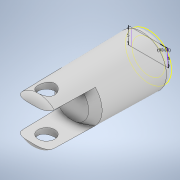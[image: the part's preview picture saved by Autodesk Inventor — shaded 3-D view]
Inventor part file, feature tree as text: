
AUTODESK INVENTOR PART (.ipt)
format: ipt  version: 2021 (Build 250183000, 183)  size: 186,880 bytes
history: native  units: mm
features: sketch x6, extrude x3, fillet x1, chamfer x1
ambient origin geometry x8: Origin, YZ Plane, XZ Plane, XY Plane, X Axis, Y Axis, Z Axis, Center Point
bodies: Solid1 (feature_tree)
feature tree (11):
  extrude  "Extrusion1"  Depth=35.0mm
  fillet  "Fillet1"  Radius=2.0mm
  sketch  "Sketch2"  dims[d4=5.0mm d5=5.0mm]
  sketch  "Sketch3"  dims[d6=90.0deg d7=5.0mm d8=0.0mm d9=0.0mm]
  extrude  "Extrusion2"  Depth=5.0mm
  extrude  "Extrusion4"  Depth=5.0mm
  chamfer  "Chamfer1"  [1 undecoded]
  sketch  "Sketch7"  dims[d16=12.0mm d17=0.0mm d18=2.0mm d19=2.0mm d20=45.0deg]
  sketch  "Sketch1"  dims[d0=15.0mm d1=35.0mm d2=-0.174533mm d3=2.0mm]
  sketch  "Sketch4"  dims[d14=5.0mm]
  sketch  "Sketch6"  dims[d15=5.0mm]
note: 1 required parameter value undecoded (feature->parameter linkage not recoverable at this tier; creation-order binding heuristic only, values carry confidence <= 0.55)
